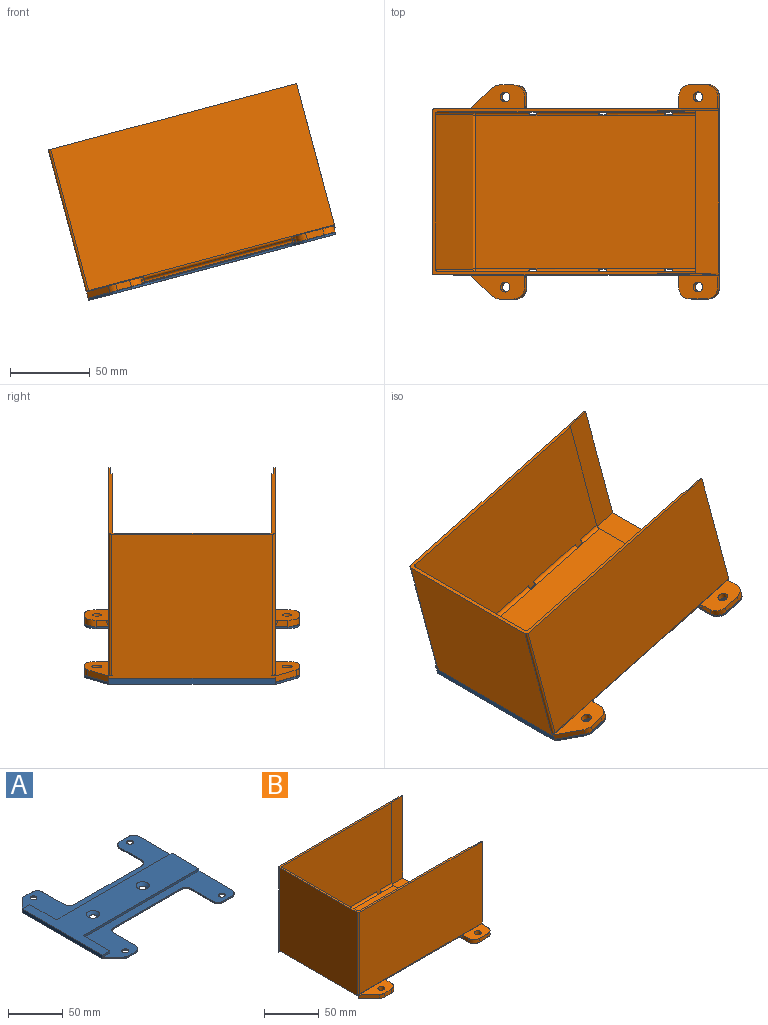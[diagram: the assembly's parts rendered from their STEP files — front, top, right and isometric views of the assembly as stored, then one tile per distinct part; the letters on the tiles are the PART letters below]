
ASSEMBLY  parts=2 mates=1
PART A: 45 faces, bbox 160x134x4 mm
  f0: plane 160x49.5mm, normal (0,0,1), area 3231.3mm2, adj f1,f9,f10,f11,f12,f13,f15,f17
  f1: plane 120x4mm, normal (1,0,0), area 267.5mm2, adj f0,f19,f20,f23,f24,f27,f29,f30
  f2: plane 11x1.5mm, normal (0,1,0), area 16.5mm2, adj f19,f20,f30,f31
  f3: plane 27.5x1.5mm, normal (-1,0,0), area 41.2mm2, adj f19,f20,f31,f35
  f4: plane 86x1.5mm, normal (0,1,0), area 129mm2, adj f19,f20,f35,f36
  f5: plane 27.5x1.5mm, normal (1,0,0), area 41.2mm2, adj f19,f20,f34,f36
  f6: plane 11.75x1.5mm, normal (0,1,0), area 17.6mm2, adj f7,f19,f20,f34
  f7: plane 16.25x15mm, normal (-0.68,0.73,0), area 33.2mm2, adj f6,f8,f19,f20
  f8: plane 104x4mm, normal (-1,0,0), area 416mm2, adj f7,f9,f20,f21,f26,f27
  f9: plane 14.24x13.14mm, normal (-0.68,-0.73,0), area 29.1mm2, adj f0,f8,f20,f32
  f10: plane 9.01x1.5mm, normal (0,-1,0), area 13.5mm2, adj f0,f20,f32,f33
  f11: plane 27.5x1.5mm, normal (1,0,0), area 41.2mm2, adj f0,f20,f33,f37
  f12: plane 86x1.5mm, normal (0,-1,0), area 129mm2, adj f0,f20,f37,f38
  f13: plane 27.5x1.5mm, normal (-1,0,0), area 41.3mm2, adj f0,f20,f28,f38
  f14: cylinder r=3.1mm len=6.2mm, axis (0,0,-1), area 29.2mm2, adj f19,f20
  f15: cylinder r=3.1mm len=6.2mm, axis (0,0,-1), area 29.2mm2, adj f0,f20
  f16: cylinder r=3.1mm len=6.2mm, axis (0,0,-1), area 29.2mm2, adj f19,f20
  f17: cylinder r=3.1mm len=6.2mm, axis (0,0,-1), area 29.2mm2, adj f0,f20
  f18: plane 11x1.5mm, normal (0,-1,0), area 16.5mm2, adj f0,f20,f28,f29
  f19: plane 160x49.5mm, normal (0,0,1), area 3232.2mm2, adj f1,f2,f3,f4,f5,f6,f7,f14
  f20: plane 160x134mm, normal (0,0,-1), area 12545.8mm2, adj f1,f2,f3,f4,f5,f6,f7,f8
  f21: plane 10x2.5mm, normal (0,-1,0), area 25mm2, adj f0,f8,f22,f27
  f22: plane 34.5x2.5mm, normal (1,0,0), area 86.2mm2, adj f0,f21,f23,f27
  f23: plane 150x2.5mm, normal (0,-1,0), area 375mm2, adj f0,f1,f22,f27
  f24: plane 150x2.5mm, normal (0,1,0), area 375mm2, adj f1,f19,f25,f27
  f25: plane 34.5x2.5mm, normal (1,0,0), area 86.2mm2, adj f19,f24,f26,f27
  f26: plane 10x2.5mm, normal (0,1,0), area 25mm2, adj f8,f19,f25,f27
  f27: plane 160x104mm, normal (0,0,1), area 6056.2mm2, adj f1,f8,f21,f22,f23,f24,f25,f26
  f28: cylinder r=7mm len=7mm, axis (0,0,1), area 16.5mm2, adj f0,f13,f18,f20
  f29: cylinder r=7mm len=7mm, axis (0,0,-1), area 16.5mm2, adj f0,f1,f18,f20
  f30: cylinder r=7mm len=7mm, axis (0,0,1), area 16.5mm2, adj f1,f2,f19,f20
  f31: cylinder r=7mm len=7mm, axis (0,0,1), area 16.5mm2, adj f2,f3,f19,f20
  f32: cylinder r=7mm len=4.75mm, axis (0,0,1), area 7.8mm2, adj f0,f9,f10,f20
  f33: cylinder r=7mm len=7mm, axis (0,0,1), area 16.5mm2, adj f0,f10,f11,f20
  f34: cylinder r=7mm len=7mm, axis (0,0,1), area 16.5mm2, adj f5,f6,f19,f20
  f35: cylinder r=7mm len=7mm, axis (0,0,1), area 16.5mm2, adj f3,f4,f19,f20
  f36: cylinder r=7mm len=7mm, axis (0,0,-1), area 16.5mm2, adj f4,f5,f19,f20
  f37: cylinder r=7mm len=7mm, axis (0,0,-1), area 16.5mm2, adj f0,f11,f12,f20
  f38: cylinder r=7mm len=7mm, axis (0,0,1), area 16.5mm2, adj f0,f12,f13,f20
  f39: cone r=3.1mm half-angle=45deg, axis (0,0,1), area 116.9mm2, adj f27,f44
  f40: cone r=3.1mm half-angle=45deg, axis (0,0,1), area 116.9mm2, adj f27,f42
  f41: cylinder r=5.75mm len=11.5mm, axis (0,0,-1), area 43.4mm2, adj f20,f42
  f42: plane 11.5x11.5mm, normal (0,0,-1), area 69.7mm2, adj f40,f41
  f43: cylinder r=5.75mm len=11.5mm, axis (0,0,-1), area 43.4mm2, adj f20,f44
  f44: plane 11.5x11.5mm, normal (0,0,-1), area 69.7mm2, adj f39,f43
PART B: 113 faces, bbox 160.9x134.1x97.4 mm
  f0: plane 142.3x96mm, normal (0,0,1), area 13660.8mm2, adj f50,f72,f73,f88
  f1: plane 96x22.5mm, normal (0,0,-1), area 2115mm2, adj f63,f65,f66,f67,f69,f70,f83,f93
  f2: plane 104x93.5mm, normal (1,0,0), area 287.3mm2, adj f4,f5,f6,f7,f51,f52,f53,f82
  f3: plane 142.3x93.5mm, normal (0,-1,0), area 12859.5mm2, adj f4,f50,f54,f56,f57,f59,f60,f62
  f4: plane 160.8x104mm, normal (0,0,1), area 813.2mm2, adj f2,f3,f6,f7,f8,f23,f37,f50
  f5: plane 160.8x104mm, normal (0,0,-1), area 6557.4mm2, adj f2,f16,f17,f23,f32,f34,f46,f47
  f6: plane 159.3x91.5mm, normal (0,-1,0), area 14575.9mm2, adj f2,f4,f83,f91
  f7: plane 159.3x91.5mm, normal (0,1,0), area 14575.9mm2, adj f2,f4,f82,f89
  f8: plane 142.3x93.5mm, normal (0,1,0), area 12859.5mm2, adj f4,f50,f63,f65,f66,f67,f69,f70
  f9: plane 160x49mm, normal (0,0,-1), area 3118.3mm2, adj f17,f18,f19,f20,f21,f22,f26,f27
  f10: plane 37.06x17.06mm, normal (0,0,1), area 365.1mm2, adj f20,f21,f22,f23,f27,f44,f45,f82
  f11: plane 27.06x15.12mm, normal (0,0,1), area 326.2mm2, adj f17,f18,f19,f26,f42,f43,f82,f99
  f12: plane 27.06x15.12mm, normal (0,0,1), area 326.2mm2, adj f14,f15,f16,f30,f40,f41,f83,f112
  f13: plane 37.06x17.06mm, normal (0,0,1), area 365.1mm2, adj f23,f24,f25,f28,f29,f38,f39,f83
  f14: plane 32.5x4.2mm, normal (-1,0,0), area 47.2mm2, adj f12,f36,f40,f78,f111,f112
  f15: plane 11x4.2mm, normal (0,-1,0), area 46.2mm2, adj f12,f36,f40,f41
  f16: plane 40x4.2mm, normal (1,0,0), area 120.8mm2, adj f5,f12,f36,f41,f75,f83
  f17: plane 40x4.2mm, normal (1,0,0), area 120.8mm2, adj f5,f9,f11,f42,f76,f82
  f18: plane 11x4.2mm, normal (0,1,0), area 46.2mm2, adj f9,f11,f42,f43
  f19: plane 32.5x4.2mm, normal (-1,0,0), area 47.2mm2, adj f9,f11,f43,f80,f99,f100
  f20: plane 32.5x4.2mm, normal (1,0,0), area 47.2mm2, adj f9,f10,f44,f81,f104,f105
  f21: plane 9.01x4.2mm, normal (0,1,0), area 37.9mm2, adj f9,f10,f44,f45
  f22: plane 14.24x13.14mm, normal (-0.68,0.73,0), area 81.4mm2, adj f9,f10,f23,f32,f45
  f23: plane 104x93.5mm, normal (-1,0,0), area 9447.9mm2, adj f4,f5,f10,f13,f22,f24,f89,f90
  f24: plane 14.24x13.14mm, normal (-0.68,-0.73,0), area 81.4mm2, adj f13,f23,f34,f36,f38
  f25: plane 9.01x4.2mm, normal (0,-1,0), area 37.9mm2, adj f13,f36,f38,f39
  f26: cylinder r=3.1mm len=6.2mm, axis (0,0,1), area 81.8mm2, adj f9,f11
  f27: cylinder r=3.1mm len=6.2mm, axis (0,0,1), area 81.8mm2, adj f9,f10
  f28: cylinder r=3.1mm len=6.2mm, axis (0,0,1), area 81.8mm2, adj f13,f36
  f29: plane 32.5x4.2mm, normal (1,0,0), area 47.2mm2, adj f13,f36,f39,f79,f106,f107
  f30: cylinder r=3.1mm len=6.2mm, axis (0,0,1), area 81.8mm2, adj f12,f36
  f31: plane 96x22.5mm, normal (0,0,-1), area 2115mm2, adj f54,f56,f57,f59,f60,f62,f82,f96
  f32: plane 10.5x2.7mm, normal (0,-1,0), area 28.4mm2, adj f5,f9,f22,f48
  f33: plane 96x0.7mm, normal (0,1,0), area 67.2mm2, adj f9,f80,f81,f102
  f34: plane 10.5x2.7mm, normal (0,1,0), area 28.4mm2, adj f5,f24,f36,f47
  f35: plane 96x0.7mm, normal (0,-1,0), area 67.2mm2, adj f36,f78,f79,f109
  f36: plane 160x49mm, normal (0,0,-1), area 3118.3mm2, adj f14,f15,f16,f24,f25,f28,f29,f30
  f37: plane 97x90.5mm, normal (1,0,0), area 8778.4mm2, adj f4,f84,f85,f86,f87,f88
  f38: cylinder r=7mm len=4.75mm, axis (0,0,-1), area 21.9mm2, adj f13,f24,f25,f36
  f39: cylinder r=7mm len=7mm, axis (0,0,-1), area 46.2mm2, adj f13,f25,f29,f36
  f40: cylinder r=7mm len=7mm, axis (0,0,-1), area 46.2mm2, adj f12,f14,f15,f36
  f41: cylinder r=7mm len=7mm, axis (0,0,1), area 46.2mm2, adj f12,f15,f16,f36
  f42: cylinder r=7mm len=7mm, axis (0,0,1), area 46.2mm2, adj f9,f11,f17,f18
  f43: cylinder r=7mm len=7mm, axis (0,0,-1), area 46.2mm2, adj f9,f11,f18,f19
  f44: cylinder r=7mm len=7mm, axis (0,0,-1), area 46.2mm2, adj f9,f10,f20,f21
  f45: cylinder r=7mm len=4.75mm, axis (0,0,1), area 21.9mm2, adj f9,f10,f21,f22
  f46: plane 145.5x2.7mm, normal (0,1,0), area 392.8mm2, adj f5,f36,f74,f75
  f47: plane 32x2.7mm, normal (-1,0,0), area 86.4mm2, adj f5,f34,f36,f74
  f48: plane 32x2.7mm, normal (-1,0,0), area 86.4mm2, adj f5,f9,f32,f77
  f49: plane 145.5x2.7mm, normal (0,-1,0), area 392.8mm2, adj f5,f9,f76,f77
  f50: plane 102x92.5mm, normal (1,0,0), area 236.7mm2, adj f0,f3,f4,f8,f51,f52,f53,f72
  f51: plane 102x15mm, normal (0,0,1), area 1530mm2, adj f2,f50,f52,f53
  f52: plane 92.5x15mm, normal (0,1,0), area 1387.5mm2, adj f2,f4,f50,f51
  f53: plane 92.5x15mm, normal (0,-1,0), area 1387.5mm2, adj f2,f4,f50,f51
  f54: plane 3.5x3mm, normal (1,0,0), area 3.6mm2, adj f3,f31,f55,f73,f98
  f55: plane 5x0.06mm, normal (0,1,0), area 0.3mm2, adj f54,f56,f73,f98
  f56: plane 3.5x3mm, normal (-1,0,0), area 3.6mm2, adj f3,f31,f55,f73,f98
  f57: plane 3.5x3mm, normal (1,0,0), area 3.6mm2, adj f3,f31,f58,f73,f97
  f58: plane 5x0.06mm, normal (0,1,0), area 0.3mm2, adj f57,f59,f73,f97
  f59: plane 3.5x3mm, normal (-1,0,0), area 3.6mm2, adj f3,f31,f58,f73,f97
  f60: plane 3.5x3mm, normal (1,0,0), area 3.6mm2, adj f3,f31,f61,f73,f96
  f61: plane 5x0.06mm, normal (0,1,0), area 0.3mm2, adj f60,f62,f73,f96
  f62: plane 3.5x3mm, normal (-1,0,0), area 3.6mm2, adj f3,f31,f61,f73,f96
  f63: plane 3.5x3mm, normal (-1,0,0), area 3.6mm2, adj f1,f8,f64,f72,f95
  f64: plane 5x0.06mm, normal (0,-1,0), area 0.3mm2, adj f63,f65,f72,f95
  f65: plane 3.5x3mm, normal (1,0,0), area 3.6mm2, adj f1,f8,f64,f72,f95
  f66: plane 3.5x3mm, normal (1,0,0), area 3.6mm2, adj f1,f8,f68,f72,f94
  f67: plane 3.5x3mm, normal (-1,0,0), area 3.6mm2, adj f1,f8,f68,f72,f94
  f68: plane 5x0.06mm, normal (0,-1,0), area 0.3mm2, adj f66,f67,f72,f94
  f69: plane 3.5x3mm, normal (1,0,0), area 3.6mm2, adj f1,f8,f71,f72,f93
  f70: plane 3.5x3mm, normal (-1,0,0), area 3.6mm2, adj f1,f8,f71,f72,f93
  f71: plane 5x0.06mm, normal (0,-1,0), area 0.3mm2, adj f69,f70,f72,f93
  f72: cylinder r=2mm len=142.3mm, axis (-1,0,0), area 407.5mm2, adj f0,f8,f50,f63,f64,f65,f66,f67
  f73: cylinder r=2mm len=142.3mm, axis (1,0,0), area 407.5mm2, adj f0,f3,f50,f54,f55,f56,f57,f58
  f74: cylinder r=2mm len=2.7mm, axis (0,0,-1), area 8.5mm2, adj f5,f36,f46,f47
  f75: cylinder r=2mm len=2.7mm, axis (0,0,1), area 8.5mm2, adj f5,f16,f36,f46
  f76: cylinder r=2mm len=2.7mm, axis (0,0,1), area 8.5mm2, adj f5,f9,f17,f49
  f77: cylinder r=2mm len=2.7mm, axis (0,0,1), area 8.5mm2, adj f5,f9,f48,f49
  f78: cylinder r=2mm len=2mm, axis (0,0,-1), area 2.2mm2, adj f14,f35,f36,f110
  f79: cylinder r=2mm len=2mm, axis (0,0,1), area 2.2mm2, adj f29,f35,f36,f108
  f80: cylinder r=2mm len=2mm, axis (0,0,-1), area 2.2mm2, adj f9,f19,f33,f101
  f81: cylinder r=2mm len=2mm, axis (0,0,1), area 2.2mm2, adj f9,f20,f33,f103
  f82: cylinder r=2mm len=159.3mm, axis (1,0,0), area 335.7mm2, adj f2,f3,f5,f7,f10,f11,f17,f31
  f83: cylinder r=2mm len=159.3mm, axis (-1,0,0), area 335.7mm2, adj f1,f2,f5,f6,f8,f12,f13,f16
  f84: cylinder r=1.5mm len=90mm, axis (0,0,-1), area 212.1mm2, adj f4,f8,f37,f86
  f85: cylinder r=1.5mm len=90mm, axis (0,0,-1), area 212.1mm2, adj f3,f4,f37,f87
  f86: torus R=0.5mm, axis (-1,0,0), area 5.4mm2, adj f37,f72,f84,f88
  f87: torus R=0.5mm, axis (-1,0,0), area 5.4mm2, adj f37,f73,f85,f88
  f88: cylinder r=1.5mm len=96mm, axis (0,1,0), area 226.2mm2, adj f0,f37,f86,f87
  f89: cylinder r=1.5mm len=91.5mm, axis (0,0,-1), area 215.6mm2, adj f4,f7,f23,f90
  f90: torus R=0.5mm, axis (1,0,0), area 1.2mm2, adj f10,f23,f82,f89
  f91: cylinder r=1.5mm len=91.5mm, axis (0,0,1), area 215.6mm2, adj f4,f6,f23,f92
  f92: torus R=0.5mm, axis (1,0,0), area 1.2mm2, adj f13,f23,f83,f91
  f93: cylinder r=1.5mm len=5mm, axis (-1,0,0), area 11.8mm2, adj f1,f69,f70,f71
  f94: cylinder r=1.5mm len=5mm, axis (-1,0,0), area 11.8mm2, adj f1,f66,f67,f68
  f95: cylinder r=1.5mm len=5mm, axis (-1,0,0), area 11.8mm2, adj f1,f63,f64,f65
  f96: cylinder r=1.5mm len=5mm, axis (1,0,0), area 11.8mm2, adj f31,f60,f61,f62
  f97: cylinder r=1.5mm len=5mm, axis (1,0,0), area 11.8mm2, adj f31,f57,f58,f59
  f98: cylinder r=1.5mm len=5mm, axis (1,0,0), area 11.8mm2, adj f31,f54,f55,f56
  f99: torus R=4mm, axis (1,0,0), area 11.9mm2, adj f11,f19,f82,f100
  f100: cylinder r=2mm len=22.5mm, axis (0,1,0), area 70.7mm2, adj f19,f31,f99,f101
  f101: sphere r=2mm, area 6.3mm2, adj f80,f100,f102
  f102: cylinder r=2mm len=96mm, axis (-1,0,0), area 301.6mm2, adj f31,f33,f101,f103
  f103: sphere r=2mm, area 6.3mm2, adj f81,f102,f104
  f104: cylinder r=2mm len=22.5mm, axis (0,-1,0), area 70.7mm2, adj f20,f31,f103,f105
  f105: torus R=4mm, axis (1,0,0), area 11.9mm2, adj f10,f20,f82,f104
  f106: torus R=4mm, axis (-1,0,0), area 11.9mm2, adj f13,f29,f83,f107
  f107: cylinder r=2mm len=22.5mm, axis (0,-1,0), area 70.7mm2, adj f1,f29,f106,f108
  f108: sphere r=2mm, area 6.3mm2, adj f79,f107,f109
  f109: cylinder r=2mm len=96mm, axis (1,0,0), area 301.6mm2, adj f1,f35,f108,f110
  f110: sphere r=2mm, area 6.3mm2, adj f78,f109,f111
  f111: cylinder r=2mm len=22.5mm, axis (0,1,0), area 70.7mm2, adj f1,f14,f110,f112
  f112: torus R=4mm, axis (-1,0,0), area 11.9mm2, adj f12,f14,f83,f111
PLACE A rot(axis=(0,-1,0),15deg) t=(-63.88,0,-15.96)mm
PLACE B rot(axis=(0,-1,0),15deg) t=(-65.3,0,-10.65)mm
MATE planar B.f5 <-> A.f27  axis (0.26,0,-0.97) through (-161.51,0,-37.99)mm
